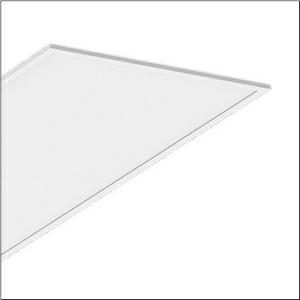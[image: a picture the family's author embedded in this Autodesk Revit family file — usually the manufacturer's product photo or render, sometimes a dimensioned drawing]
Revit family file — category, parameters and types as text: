
# Revit family: apollon_21_linear_51mq19wd2m14
name_source: partatom
category: Lighting Fixtures
units: mm (PartAtom-declared; Revit-internal decimal feet)

## family parameters
Cut with Voids When Loaded = No
Host = Face
Light Source = No
Part Type = Normal
Room Calculation Point = No
Round Connector Dimension = Use Diameter
Shared = No

## types (1)
- --- (1 x LED, 7000 lm, 44.6 W, 4000K)
    Apparent Load = 45 VA
    CIE Flux Codes = 60 87 97 100 100
    Color Rendering = 80
    Color Temperature = 4000K
    Default Elevation = 1800 mm
    Description = Apollon 21 linear, office luminaire, primary optical cover: micro prismatic cover, of PMMA, CAT 2 (L<= 3000cd/m²), light emission: direct distribution, primary light characteristic: symmetric, installation type: lay-in mounting, recessed, LED, rated luminous flux: 7.820lm, luminous efficacy: 173lm/W, light colour: 830/840, colour temperature: 3000/4000K, control gear: DALI 2, Multilumen, with terminal, 5-pole, mains connection: 220..240V, AC/DC, 0/50..60Hz, rated input power: 45.3W, suitable for self-contained emergency lighting element 59MQE002602A with integrated self-test function according to EN 60598-2-22, housing, of aluminium, coated, traffic white (RAL 9016), module: M625, length: 1.245mm, width: 622mm, height: 55mm, housing upper side, of sheet steel, galvanised, protection rating (complete): IP20, protection rating (lamp compartment, on room side): IP50, insulation class (complete): insulation class II (safety insulation), certification: CE, ENEC, UKCA, impact resistance: IK03, permissible operating ambient temperature: -20..+45°C, standard: EN 60598-2-22, corresponds to IFS (International Featured Standards) requirements for safety and quality in the food industry, packaging unit: 1 piece
    Height = 0 mm  [stored 0 ft]
    Lamp = 1 x LED
    Lamp Light Flux = 7000 lm
    Lamp Power = 44.6 W
    Lamp count = 1
    Length = 1245 mm
    Luminous efficacy = 157 lm/W
    Manufacturer = Siteco
    ModVariant = No
    Model = 51MQ19WD2M14
    Mounting Place = Ceiling
    Mounting Type = Recessed
    Number of Poles = 1
    OnlyDefault = Yes
    Power Factor = 1
    Product Name = Apollon 21 linear
    Product group = office luminaire | ceiling recessed
    ProductGroupID = 400
    Protection Class = Protection class II
    Protection Degree = IP 20
    RLX_Detail_Level = 1
    RLX_Emergency_Light_Flux = 0 lm
    RLX_Emergency_Type = 0
    RLX_Emergency_Type_DB = No
    RlxData = <blob elided: 19865 chars, md5=371e71dd>
    Socket = socket
    Standby Power = 0 W
    System Light Flux = 7000 lm
    System Power = 45 W
    Type Comments = factory setting
    Type Image = l_1335551.jpg
    URL = http://relux.com
    VarID = @adj_075839
    Voltage = 0 V
    Weight = 0.00 kg
    Width = 622 mm

note: [stored X ft] marks values corroborated as IEEE doubles in the binary element streams (Revit-internal decimal feet)

## geometry (parser evidence)
native form markers: Blend x4, Sweep x12
no freeform markers — native parametric forms only
